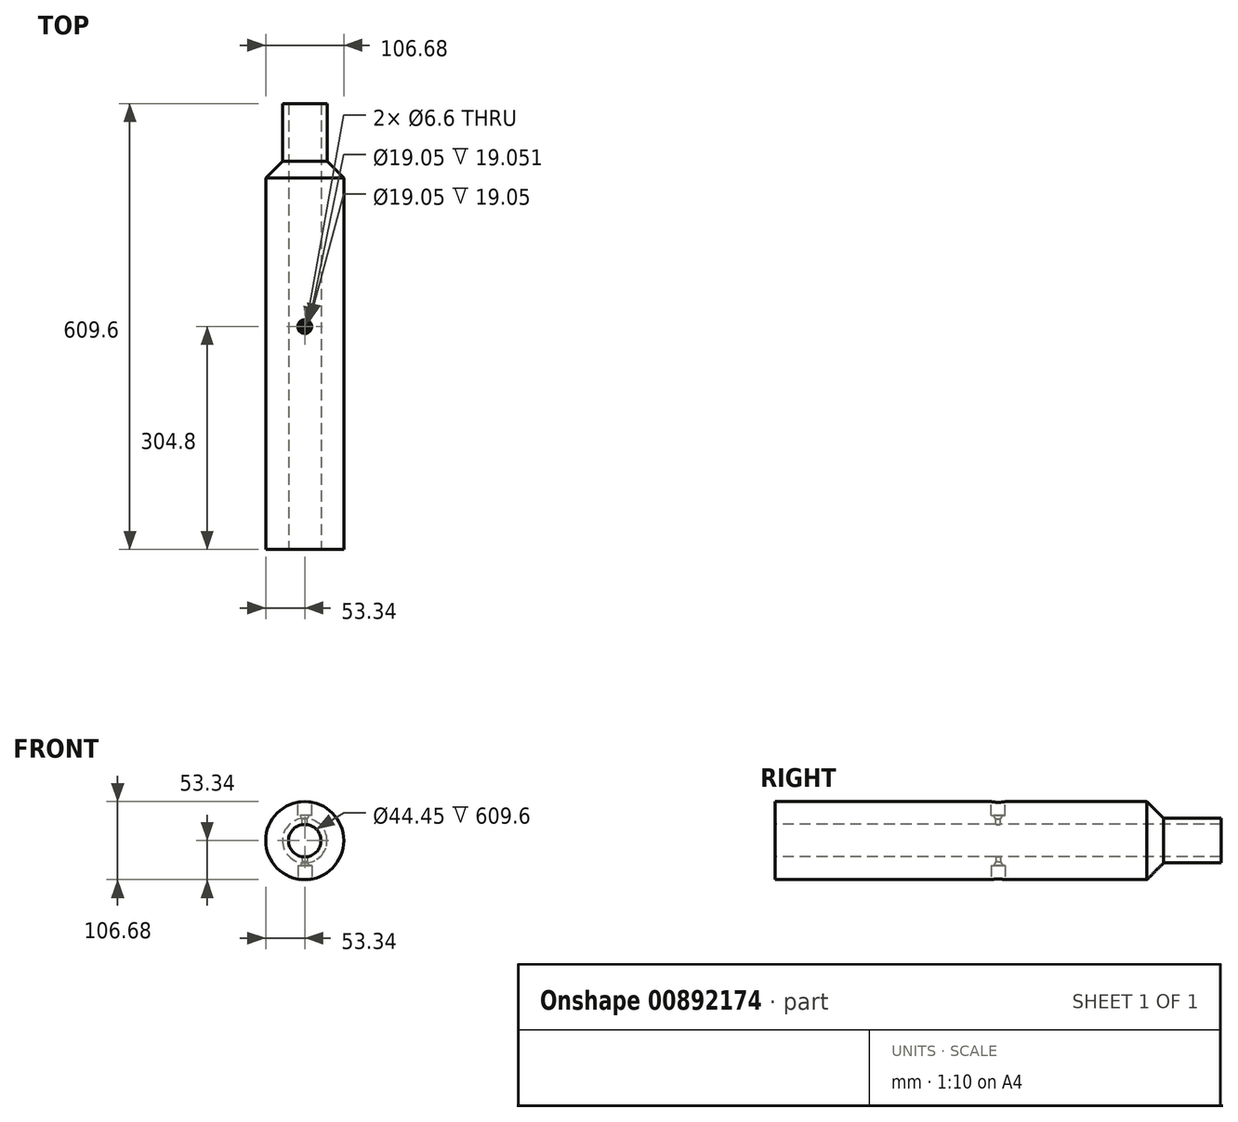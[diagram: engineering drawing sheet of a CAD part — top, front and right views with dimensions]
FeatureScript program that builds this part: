
annotation { "Feature Type Name" : "Feature", "Feature Type Description" : "" }
export const myFeature = defineFeature(function(context is Context, id is Id, definition is map)
    precondition{}
    {
        {
            var Q0;
            Q0=qCreatedBy(makeId("Front.planeOp"),FACE);
            var sketch = newSketch(context, id + "F0", { "sketchPlane" : qUnion([Q0])});
            skCircle(sketch, "E0", {"center": v(0, 0) * mm, "radius": 22.23 * mm});
            skCircle(sketch, "E1", {"center": v(0, 0) * mm, "radius": 53.34 * mm});
            skSolve(sketch);
        }
        {
            var Q0;
            Q0=makeQuery(id+"F0.imprint","IMPRINT",FACE,{"disambiguationData":[TD([[makeQuery(id+"F0.imprint","IMPRINT",EDGE,{"derivedFrom":sQuery(id+"F0.wireOp",EDGE,"E0")}),-1.0]])]});
            extrude(context, id + "F1", {"entities" : qUnion([Q0]), "endBound" : BoundingType.SYMMETRIC, "oppositeDirection" : true, "depth" : 609.6 * mm, "offsetDistance" : 25.4 * mm});
        }
        {
            var Q0;
            Q0=makeQuery(id+"F1.opExtrude","CAP_FACE",FACE,{"disambiguationData":[OSD([sQuery(id+"F0.wireOp",EDGE,"E0"),sQuery(id+"F0.wireOp",EDGE,"E1")])],"isStart":false});
            cPlane(context, id + "F2", {"entities" : qUnion([Q0]), "cplaneType" : CPlaneType.OFFSET, "offset" : 0 * mm, "oppositeDirection" : true, "width" : 152.4 * mm, "height" : 152.4 * mm});
        }
        {
            var Q0;
            Q0=qCreatedBy(makeId("Front.planeOp"),FACE);
            cPlane(context, id + "F3", {"entities" : qUnion([Q0]), "cplaneType" : CPlaneType.OFFSET, "offset" : 203.2 * mm, "oppositeDirection" : true, "width" : 152.4 * mm, "height" : 152.4 * mm});
        }
        {
            var Q0;
            Q0=qCreatedBy(id+"F2.planeOp",FACE);
            var sketch = newSketch(context, id + "F4", { "sketchPlane" : qUnion([Q0])});
            skCircle(sketch, "E2", {"center": v(0, 0) * mm, "radius": 22.23 * mm});
            skCircle(sketch, "E3", {"center": v(0, 0) * mm, "radius": 30.48 * mm});
            skCircle(sketch, "E4", {"center": v(0, 0) * mm, "radius": 53.34 * mm});
            skSolve(sketch);
        }
        {
            var Q0;
            Q0=makeQuery(id+"F4.imprint","IMPRINT",FACE,{"disambiguationData":[TD([[makeQuery(id+"F4.imprint","IMPRINT",EDGE,{"derivedFrom":sQuery(id+"F4.wireOp",EDGE,"E3")}),-1.0]])]});
            var Q1;
            Q1=qCreatedBy(id+"F3.planeOp",FACE);
            extrude(context, id + "F5", {"entities" : qUnion([Q0]), "operationType" : NewBodyOperationType.REMOVE, "oppositeDirection" : true, "depth" : 101.6 * mm, "endBoundEntityFace" : qUnion([Q1]), "offsetDistance" : 25.4 * mm});
        }
        {
            var Q0;
            Q0=qCreatedBy(makeId("Right.planeOp"),FACE);
            var sketch = newSketch(context, id + "F6", { "sketchPlane" : qUnion([Q0])});
            skLineSegment(sketch, "E5", {"start": v(0, 0) * mm, "end": v(203.2, 0) * mm, "construction": true});
            skLineSegment(sketch, "E6", {"start": v(203.2, 0) * mm, "end": v(203.2, 53.34) * mm});
            skLineSegment(sketch, "E7", {"start": v(203.2, 0) * mm, "end": v(203.2, 30.48) * mm});
            skLineSegment(sketch, "E8", {"start": v(203.2, 30.48) * mm, "end": v(226.06, 30.48) * mm});
            skLineSegment(sketch, "E9", {"start": v(226.06, 30.48) * mm, "end": v(203.2, 53.34) * mm});
            skSolve(sketch);
        }
        {
            var Q0;
            Q0=makeQuery(id+"F6.imprint","IMPRINT",FACE,{"disambiguationData":[TD([[makeQuery(id+"F6.imprint","IMPRINT",EDGE,{"derivedFrom":sQuery(id+"F6.wireOp",EDGE,"E6")}),-1.0]])]});
            var Q1;
            Q1=sQuery(id+"F6.wireOp",EDGE,"E5");
            revolve(context, id + "F7", {"operationType" : NewBodyOperationType.ADD, "surfaceOperationType" : NewSurfaceOperationType.NEW, "entities" : qUnion([Q0]), "axis" : qUnion([Q1]), "revolveType" : RevolveType.FULL});
        }
        {
            var Q0;
            Q0=qCreatedBy(makeId("Top.planeOp"),FACE);
            cPlane(context, id + "F8", {"entities" : qUnion([Q0]), "cplaneType" : CPlaneType.OFFSET, "offset" : 53.34 * mm, "width" : 152.4 * mm, "height" : 152.4 * mm});
        }
        {
            var Q0;
            Q0=qCreatedBy(makeId("Top.planeOp"),FACE);
            cPlane(context, id + "F9", {"entities" : qUnion([Q0]), "cplaneType" : CPlaneType.OFFSET, "offset" : 53.34 * mm, "oppositeDirection" : true, "width" : 152.4 * mm, "height" : 152.4 * mm});
        }
        {
            var Q0;
            Q0=qCreatedBy(id+"F8.planeOp",FACE);
            var sketch = newSketch(context, id + "F10", { "sketchPlane" : qUnion([Q0])});
            skCircle(sketch, "E10", {"center": v(0, 0) * mm, "radius": 9.53 * mm});
            skCircle(sketch, "E11", {"center": v(0, 0) * mm, "radius": 3.3 * mm});
            skSolve(sketch);
        }
        {
            var Q0;
            Q0=makeQuery(id+"F10.imprint","IMPRINT",FACE,{"disambiguationData":[TD([[makeQuery(id+"F10.imprint","IMPRINT",EDGE,{"derivedFrom":sQuery(id+"F10.wireOp",EDGE,"E10")}),1.0]])]});
            var Q1;
            Q1=makeQuery(id+"F10.imprint","IMPRINT",FACE,{"disambiguationData":[TD([[makeQuery(id+"F10.imprint","IMPRINT",EDGE,{"derivedFrom":sQuery(id+"F10.wireOp",EDGE,"E11")}),1.0]])]});
            extrude(context, id + "F11", {"entities" : qUnion([Q0, Q1]), "operationType" : NewBodyOperationType.REMOVE, "oppositeDirection" : true, "depth" : 19.05 * mm, "offsetDistance" : 25.4 * mm});
        }
        {
            var Q0;
            Q0=makeQuery(id+"F10.imprint","IMPRINT",FACE,{"disambiguationData":[TD([[makeQuery(id+"F10.imprint","IMPRINT",EDGE,{"derivedFrom":sQuery(id+"F10.wireOp",EDGE,"E11")}),1.0]])]});
            var Q1;
            Q1=makeQuery(id+"F1.opExtrude","SWEPT_FACE",FACE,{"disambiguationData":[OSD([sQuery(id+"F0.wireOp",EDGE,"E0")])]});
            extrude(context, id + "F12", {"entities" : qUnion([Q0]), "operationType" : NewBodyOperationType.REMOVE, "endBound" : BoundingType.UP_TO_SURFACE, "oppositeDirection" : true, "depth" : 27.94 * mm, "endBoundEntityFace" : qUnion([Q1]), "offsetDistance" : 25.4 * mm});
        }
        {
            var Q0;
            Q0=qCreatedBy(id+"F9.planeOp",FACE);
            var sketch = newSketch(context, id + "F13", { "sketchPlane" : qUnion([Q0])});
            skCircle(sketch, "E12", {"center": v(0, 0) * mm, "radius": 9.53 * mm});
            skCircle(sketch, "E13", {"center": v(0, 0) * mm, "radius": 3.3 * mm});
            skSolve(sketch);
        }
        {
            var Q0;
            Q0=makeQuery(id+"F13.imprint","IMPRINT",FACE,{"disambiguationData":[TD([[makeQuery(id+"F13.imprint","IMPRINT",EDGE,{"derivedFrom":sQuery(id+"F13.wireOp",EDGE,"E12")}),1.0]])]});
            var Q1;
            Q1=makeQuery(id+"F13.imprint","IMPRINT",FACE,{"disambiguationData":[TD([[makeQuery(id+"F13.imprint","IMPRINT",EDGE,{"derivedFrom":sQuery(id+"F13.wireOp",EDGE,"E13")}),1.0]])]});
            extrude(context, id + "F14", {"entities" : qUnion([Q0, Q1]), "operationType" : NewBodyOperationType.REMOVE, "depth" : 19.05 * mm, "offsetDistance" : 25.4 * mm});
        }
        {
            var Q0;
            Q0=makeQuery(id+"F13.imprint","IMPRINT",FACE,{"disambiguationData":[TD([[makeQuery(id+"F13.imprint","IMPRINT",EDGE,{"derivedFrom":sQuery(id+"F13.wireOp",EDGE,"E13")}),1.0]])]});
            var Q1;
            Q1=makeQuery(id+"F1.opExtrude","SWEPT_FACE",FACE,{"disambiguationData":[OSD([sQuery(id+"F0.wireOp",EDGE,"E0")])]});
            extrude(context, id + "F15", {"entities" : qUnion([Q0]), "operationType" : NewBodyOperationType.REMOVE, "endBound" : BoundingType.UP_TO_SURFACE, "depth" : 27.94 * mm, "endBoundEntityFace" : qUnion([Q1]), "offsetDistance" : 25.4 * mm});
        }
        {
            var Q0;
            Q0=qCreatedBy(makeId("Right.planeOp"),FACE);
            var sketch = newSketch(context, id + "F16", { "sketchPlane" : qUnion([Q0])});
            skLineSegment(sketch, "E14", {"start": v(0, 0) * mm, "end": v(0, 34.3) * mm, "construction": true});
            skLineSegment(sketch, "E15", {"start": v(3.3, 34.3) * mm, "end": v(6.35, 34.3) * mm});
            skLineSegment(sketch, "E16", {"start": v(0, 0) * mm, "end": v(3.3, 0) * mm, "construction": true});
            skLineSegment(sketch, "E17", {"start": v(3.3, 29.21) * mm, "end": v(6.35, 34.3) * mm});
            skLineSegment(sketch, "E18", {"start": v(3.3, 29.21) * mm, "end": v(3.3, 34.3) * mm});
            skLineSegment(sketch, "E19.MirrorCS", {"start": v(3.3, -29.21) * mm, "end": v(3.3, -34.3) * mm});
            skLineSegment(sketch, "E20.MirrorCS", {"start": v(3.3, -34.3) * mm, "end": v(6.35, -34.3) * mm});
            skLineSegment(sketch, "E21.MirrorCS", {"start": v(3.3, -29.21) * mm, "end": v(6.35, -34.3) * mm});
            skSolve(sketch);
        }
        {
            var Q0;
            Q0 = qSketchRegion(id + "F16", true);
            var Q1;
            Q1=sQuery(id+"F16.wireOp",EDGE,"E14");
            revolve(context, id + "F17", {"operationType" : NewBodyOperationType.REMOVE, "surfaceOperationType" : NewSurfaceOperationType.NEW, "entities" : qUnion([Q0]), "axis" : qUnion([Q1]), "revolveType" : RevolveType.FULL, "oppositeDirection" : true});
        }
    });
